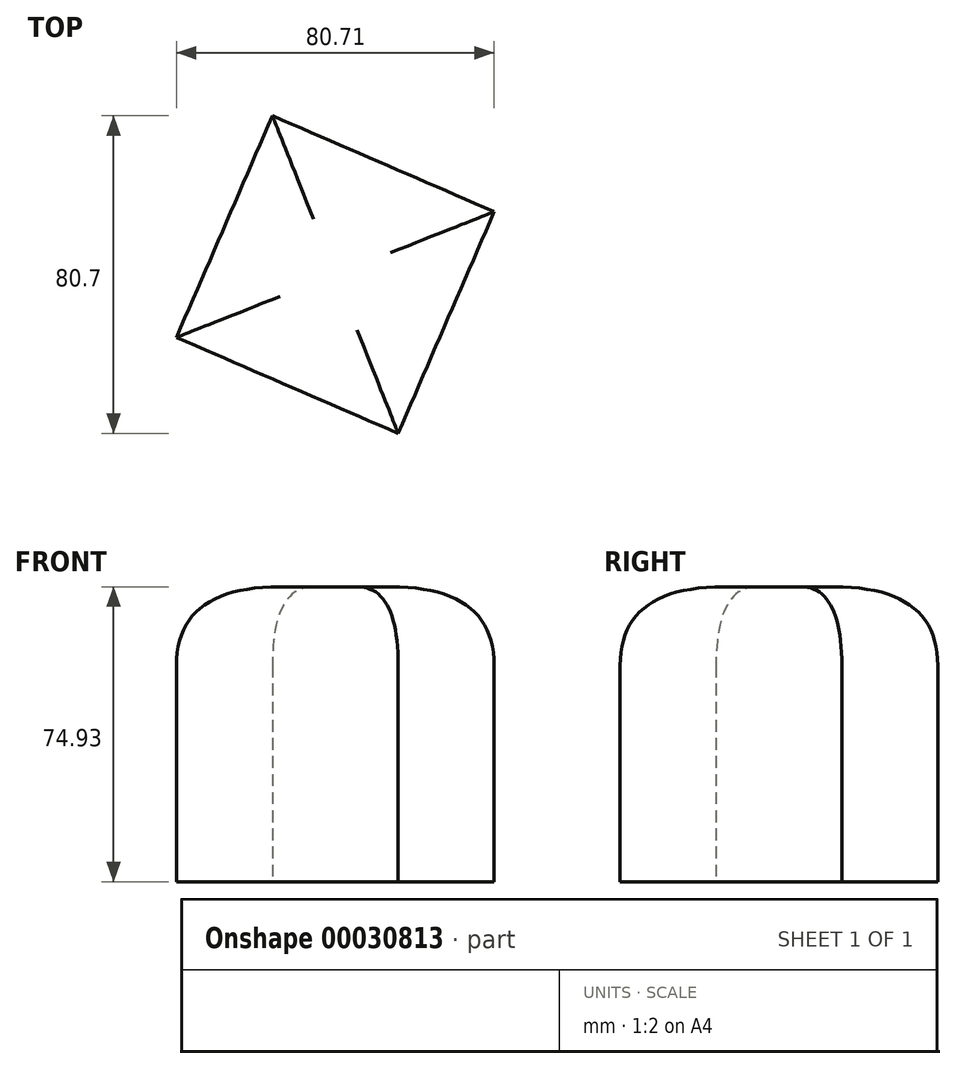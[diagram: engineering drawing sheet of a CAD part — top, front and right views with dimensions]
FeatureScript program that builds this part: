
annotation { "Feature Type Name" : "Feature", "Feature Type Description" : "" }
export const myFeature = defineFeature(function(context is Context, id is Id, definition is map)
    precondition{}
    {
        {
            var Q0;
            Q0=qCreatedBy(makeId("Top.planeOp"),FACE);
            var sketch = newSketch(context, id + "F0", { "sketchPlane" : qUnion([Q0])});
            skLineSegment(sketch, "E0.bottom", {"start": v(-35.94, 30.05) * mm, "end": v(30.9, 30.05) * mm});
            skLineSegment(sketch, "E0.top", {"start": v(-35.94, -31.31) * mm, "end": v(30.9, -31.31) * mm});
            skLineSegment(sketch, "E0.left", {"start": v(-35.94, 30.05) * mm, "end": v(-35.94, -31.31) * mm});
            skLineSegment(sketch, "E0.right", {"start": v(30.9, 30.05) * mm, "end": v(30.9, -31.31) * mm});
            skCircle(sketch, "E1.cCircle", {"center": v(-72.09, 37.2) * mm, "radius": 30.69 * mm, "construction": true});
            skLineSegment(sketch, "E1.0", {"start": v(-31.73, 53.17) * mm, "end": v(-56.11, -3.15) * mm});
            skLineSegment(sketch, "E1.1", {"start": v(-56.11, -3.15) * mm, "end": v(-112.44, 21.23) * mm});
            skLineSegment(sketch, "E1.2", {"start": v(-112.44, 21.23) * mm, "end": v(-88.06, 77.55) * mm});
            skLineSegment(sketch, "E1.3", {"start": v(-88.06, 77.55) * mm, "end": v(-31.73, 53.17) * mm});
            skPoint(sketch, "E1.0.midPoint", {"position": v(-43.92, 25) * mm});
            skSolve(sketch);
        }
        {
            var Q0;
            Q0=makeQuery(id+"F0.imprint","IMPRINT",FACE,{"disambiguationData":[TD([[makeQuery(id+"F0.imprint","IMPRINT",EDGE,{"derivedFrom":sQuery(id+"F0.wireOp",EDGE,"E1.0")}),-1.0]])]});
            extrude(context, id + "F1", {"entities" : qUnion([Q0]), "depth" : 74.93 * mm});
        }
        {
            var Q0;
            Q0=makeQuery(id+"F1.opExtrude","CAP_FACE",FACE,{"disambiguationData":[OSD([sQuery(id+"F0.wireOp",EDGE,"E1.0"),sQuery(id+"F0.wireOp",EDGE,"E1.1"),sQuery(id+"F0.wireOp",EDGE,"E1.2"),sQuery(id+"F0.wireOp",EDGE,"E1.3")])],"isStart":false});
            fillet(context, id + "F2", {"entities" : qUnion([Q0]), "radius" : 20 * mm, "tangentPropagation" : true, "rho" : 0.5, "crossSection" : FilletCrossSection.CONIC, "allowEdgeOverflow" : false});
        }
    });
